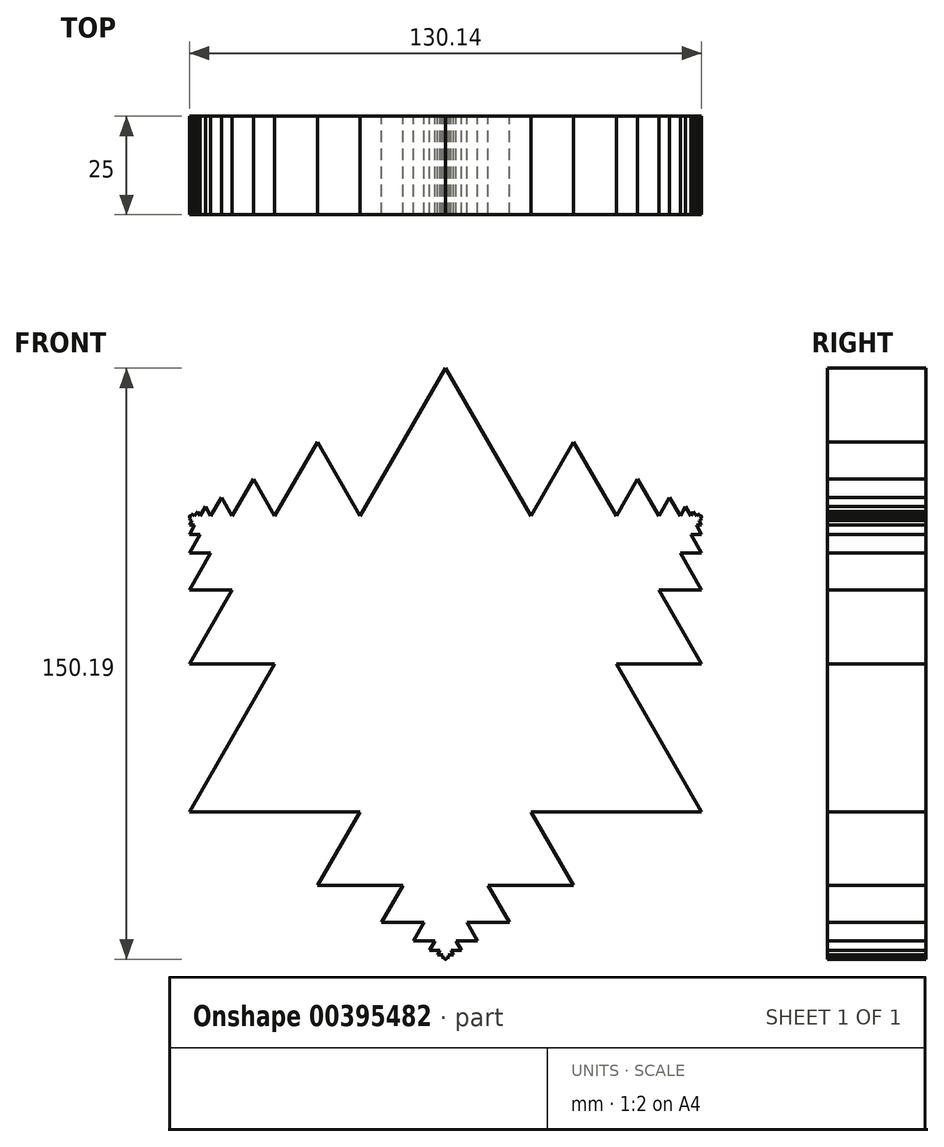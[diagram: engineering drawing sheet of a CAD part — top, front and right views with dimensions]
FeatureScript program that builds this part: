
annotation { "Feature Type Name" : "Feature", "Feature Type Description" : "" }
export const myFeature = defineFeature(function(context is Context, id is Id, definition is map)
    precondition{}
    {
        {
            var Q0;
            Q0=qCreatedBy(makeId("Front.planeOp"),FACE);
            var sketch = newSketch(context, id + "F0", { "sketchPlane" : qUnion([Q0])});
            skLineSegment(sketch, "E0.0", {"start": v(0, 75.13) * mm, "end": v(65.07, -37.57) * mm});
            skLineSegment(sketch, "E0.1", {"start": v(65.07, -37.57) * mm, "end": v(-65.07, -37.57) * mm});
            skLineSegment(sketch, "E0.2", {"start": v(-65.07, -37.57) * mm, "end": v(0, 75.13) * mm});
            skLineSegment(sketch, "E1.0", {"start": v(0, 0) * mm, "end": v(-65.07, 0) * mm});
            skLineSegment(sketch, "E1.1", {"start": v(-65.07, 0) * mm, "end": v(-32.53, 56.35) * mm});
            skLineSegment(sketch, "E1.2", {"start": v(-32.53, 56.35) * mm, "end": v(0, 0) * mm});
            skLineSegment(sketch, "E2.0", {"start": v(0, 0) * mm, "end": v(32.53, -56.35) * mm});
            skLineSegment(sketch, "E2.1", {"start": v(32.53, -56.35) * mm, "end": v(-32.53, -56.35) * mm});
            skLineSegment(sketch, "E2.2", {"start": v(-32.53, -56.35) * mm, "end": v(0, 0) * mm});
            skLineSegment(sketch, "E3.0", {"start": v(0, 0) * mm, "end": v(32.53, 56.35) * mm});
            skLineSegment(sketch, "E3.1", {"start": v(32.53, 56.35) * mm, "end": v(65.07, 0) * mm});
            skLineSegment(sketch, "E3.2", {"start": v(65.07, 0) * mm, "end": v(0, 0) * mm});
            skPoint(sketch, "E2.cCircle.center.orphan", {"position": v(0, -37.57) * mm});
            skPoint(sketch, "E3.cCircle.center.orphan", {"position": v(32.53, 18.78) * mm});
            skPoint(sketch, "E1.cCircle.center.orphan", {"position": v(-32.53, 18.78) * mm});
            skLineSegment(sketch, "E4.0", {"start": v(-32.53, 18.78) * mm, "end": v(-65.07, 18.78) * mm});
            skLineSegment(sketch, "E4.1", {"start": v(-65.07, 18.78) * mm, "end": v(-48.8, 46.96) * mm});
            skLineSegment(sketch, "E4.2", {"start": v(-48.8, 46.96) * mm, "end": v(-32.53, 18.78) * mm});
            skLineSegment(sketch, "E5.0", {"start": v(-32.53, 18.78) * mm, "end": v(-16.27, 46.96) * mm});
            skLineSegment(sketch, "E5.1", {"start": v(-16.27, 46.96) * mm, "end": v(0, 18.78) * mm});
            skLineSegment(sketch, "E5.2", {"start": v(0, 18.78) * mm, "end": v(-32.53, 18.78) * mm});
            skLineSegment(sketch, "E6.0", {"start": v(-32.53, 18.78) * mm, "end": v(-16.27, -9.4) * mm});
            skLineSegment(sketch, "E6.1", {"start": v(-16.27, -9.4) * mm, "end": v(-48.8, -9.4) * mm});
            skLineSegment(sketch, "E6.2", {"start": v(-48.8, -9.4) * mm, "end": v(-32.53, 18.78) * mm});
            skLineSegment(sketch, "E7.0", {"start": v(0, -37.57) * mm, "end": v(16.27, -65.74) * mm});
            skLineSegment(sketch, "E7.1", {"start": v(16.27, -65.74) * mm, "end": v(-16.27, -65.74) * mm});
            skLineSegment(sketch, "E7.2", {"start": v(-16.27, -65.74) * mm, "end": v(0, -37.57) * mm});
            skLineSegment(sketch, "E8.0", {"start": v(0, -37.57) * mm, "end": v(-32.53, -37.57) * mm});
            skLineSegment(sketch, "E8.1", {"start": v(-32.53, -37.57) * mm, "end": v(-16.27, -9.4) * mm});
            skLineSegment(sketch, "E8.2", {"start": v(-16.27, -9.4) * mm, "end": v(0, -37.57) * mm});
            skLineSegment(sketch, "E9.0", {"start": v(0, -37.57) * mm, "end": v(16.27, -9.4) * mm});
            skLineSegment(sketch, "E9.1", {"start": v(16.27, -9.4) * mm, "end": v(32.53, -37.57) * mm});
            skLineSegment(sketch, "E9.2", {"start": v(32.53, -37.57) * mm, "end": v(0, -37.57) * mm});
            skLineSegment(sketch, "E10.0", {"start": v(32.53, 18.78) * mm, "end": v(48.8, -9.4) * mm});
            skLineSegment(sketch, "E10.1", {"start": v(48.8, -9.4) * mm, "end": v(16.27, -9.4) * mm});
            skLineSegment(sketch, "E10.2", {"start": v(16.27, -9.4) * mm, "end": v(32.53, 18.78) * mm});
            skLineSegment(sketch, "E11.0", {"start": v(32.53, 18.78) * mm, "end": v(0, 18.78) * mm});
            skLineSegment(sketch, "E11.1", {"start": v(0, 18.78) * mm, "end": v(16.27, 46.96) * mm});
            skLineSegment(sketch, "E11.2", {"start": v(16.27, 46.96) * mm, "end": v(32.53, 18.78) * mm});
            skLineSegment(sketch, "E12.0", {"start": v(32.53, 18.78) * mm, "end": v(48.8, 46.96) * mm});
            skLineSegment(sketch, "E12.1", {"start": v(48.8, 46.96) * mm, "end": v(65.07, 18.78) * mm});
            skLineSegment(sketch, "E12.2", {"start": v(65.07, 18.78) * mm, "end": v(32.53, 18.78) * mm});
            skPoint(sketch, "E4.cCircle.center.orphan", {"position": v(-48.8, 28.18) * mm});
            skPoint(sketch, "E12.cCircle.center.orphan", {"position": v(48.8, 28.18) * mm});
            skPoint(sketch, "E11.cCircle.center.orphan", {"position": v(16.27, 28.18) * mm});
            skPoint(sketch, "E5.cCircle.center.orphan", {"position": v(-16.27, 28.18) * mm});
            skPoint(sketch, "E6.cCircle.center.orphan", {"position": v(-32.53, 0) * mm});
            skPoint(sketch, "E7.cCircle.center.orphan", {"position": v(0, -56.35) * mm});
            skPoint(sketch, "E10.cCircle.center.orphan", {"position": v(32.53, 0) * mm});
            skPoint(sketch, "E9.cCircle.center.orphan", {"position": v(16.27, -28.18) * mm});
            skPoint(sketch, "E8.cCircle.center.orphan", {"position": v(-16.27, -28.18) * mm});
            skCircle(sketch, "E13.cCircle", {"center": v(-56.93, 32.87) * mm, "radius": 9.4 * mm, "construction": true});
            skLineSegment(sketch, "E13.0", {"start": v(-48.8, 28.18) * mm, "end": v(-65.07, 28.18) * mm});
            skLineSegment(sketch, "E13.1", {"start": v(-65.07, 28.18) * mm, "end": v(-56.93, 42.26) * mm});
            skLineSegment(sketch, "E13.2", {"start": v(-56.93, 42.26) * mm, "end": v(-48.8, 28.18) * mm});
            skCircle(sketch, "E14.cCircle", {"center": v(0, -65.74) * mm, "radius": 9.4 * mm, "construction": true});
            skLineSegment(sketch, "E14.0", {"start": v(0, -56.35) * mm, "end": v(8.13, -70.44) * mm});
            skLineSegment(sketch, "E14.1", {"start": v(8.13, -70.44) * mm, "end": v(-8.13, -70.44) * mm});
            skLineSegment(sketch, "E14.2", {"start": v(-8.13, -70.44) * mm, "end": v(0, -56.35) * mm});
            skCircle(sketch, "E15.cCircle", {"center": v(56.93, 32.87) * mm, "radius": 9.4 * mm, "construction": true});
            skLineSegment(sketch, "E15.0", {"start": v(48.8, 28.18) * mm, "end": v(56.93, 42.26) * mm});
            skLineSegment(sketch, "E15.1", {"start": v(56.93, 42.26) * mm, "end": v(65.07, 28.18) * mm});
            skLineSegment(sketch, "E15.2", {"start": v(65.07, 28.18) * mm, "end": v(48.8, 28.18) * mm});
            skCircle(sketch, "E16.cCircle", {"center": v(-61, 35.22) * mm, "radius": 4.7 * mm, "construction": true});
            skLineSegment(sketch, "E16.0", {"start": v(-56.93, 32.87) * mm, "end": v(-65.07, 32.87) * mm});
            skLineSegment(sketch, "E16.1", {"start": v(-65.07, 32.87) * mm, "end": v(-61, 39.92) * mm});
            skLineSegment(sketch, "E16.2", {"start": v(-61, 39.92) * mm, "end": v(-56.93, 32.87) * mm});
            skCircle(sketch, "E17.cCircle", {"center": v(-63.04, 36.4) * mm, "radius": 2.35 * mm, "construction": true});
            skLineSegment(sketch, "E17.0", {"start": v(-61, 35.22) * mm, "end": v(-65.07, 35.22) * mm});
            skLineSegment(sketch, "E17.1", {"start": v(-65.07, 35.22) * mm, "end": v(-63.04, 38.74) * mm});
            skLineSegment(sketch, "E17.2", {"start": v(-63.04, 38.74) * mm, "end": v(-61, 35.22) * mm});
            skCircle(sketch, "E18.cCircle", {"center": v(-64.05, 36.98) * mm, "radius": 1.17 * mm, "construction": true});
            skLineSegment(sketch, "E18.0", {"start": v(-63.04, 36.4) * mm, "end": v(-65.07, 36.4) * mm});
            skLineSegment(sketch, "E18.1", {"start": v(-65.07, 36.4) * mm, "end": v(-64.05, 38.15) * mm});
            skLineSegment(sketch, "E18.2", {"start": v(-64.05, 38.15) * mm, "end": v(-63.04, 36.4) * mm});
            skCircle(sketch, "E19.cCircle", {"center": v(-64.56, 37.27) * mm, "radius": 0.59 * mm, "construction": true});
            skLineSegment(sketch, "E19.0", {"start": v(-64.05, 36.98) * mm, "end": v(-65.07, 36.98) * mm});
            skLineSegment(sketch, "E19.1", {"start": v(-65.07, 36.98) * mm, "end": v(-64.56, 37.86) * mm});
            skLineSegment(sketch, "E19.2", {"start": v(-64.56, 37.86) * mm, "end": v(-64.05, 36.98) * mm});
            skCircle(sketch, "E20.cCircle", {"center": v(-64.81, 37.42) * mm, "radius": 0.3 * mm, "construction": true});
            skLineSegment(sketch, "E20.0", {"start": v(-64.56, 37.27) * mm, "end": v(-65.07, 37.27) * mm});
            skLineSegment(sketch, "E20.1", {"start": v(-65.07, 37.27) * mm, "end": v(-64.81, 37.71) * mm});
            skLineSegment(sketch, "E20.2", {"start": v(-64.81, 37.71) * mm, "end": v(-64.56, 37.27) * mm});
            skCircle(sketch, "E21.cCircle", {"center": v(-64.94, 37.5) * mm, "radius": 0.15 * mm, "construction": true});
            skLineSegment(sketch, "E21.0", {"start": v(-64.81, 37.42) * mm, "end": v(-65.07, 37.42) * mm});
            skLineSegment(sketch, "E21.1", {"start": v(-65.07, 37.42) * mm, "end": v(-64.94, 37.64) * mm});
            skLineSegment(sketch, "E21.2", {"start": v(-64.94, 37.64) * mm, "end": v(-64.81, 37.42) * mm});
            skCircle(sketch, "E22.cCircle", {"center": v(0, -70.44) * mm, "radius": 4.7 * mm, "construction": true});
            skLineSegment(sketch, "E22.0", {"start": v(0, -65.74) * mm, "end": v(4.07, -72.79) * mm});
            skLineSegment(sketch, "E22.1", {"start": v(4.07, -72.79) * mm, "end": v(-4.07, -72.79) * mm});
            skLineSegment(sketch, "E22.2", {"start": v(-4.07, -72.79) * mm, "end": v(0, -65.74) * mm});
            skCircle(sketch, "E23.cCircle", {"center": v(0, -72.79) * mm, "radius": 2.35 * mm, "construction": true});
            skLineSegment(sketch, "E23.0", {"start": v(0, -70.44) * mm, "end": v(2.03, -73.96) * mm});
            skLineSegment(sketch, "E23.1", {"start": v(2.03, -73.96) * mm, "end": v(-2.03, -73.96) * mm});
            skLineSegment(sketch, "E23.2", {"start": v(-2.03, -73.96) * mm, "end": v(0, -70.44) * mm});
            skCircle(sketch, "E24.cCircle", {"center": v(0, -73.96) * mm, "radius": 1.17 * mm, "construction": true});
            skLineSegment(sketch, "E24.0", {"start": v(0, -72.79) * mm, "end": v(1.02, -74.55) * mm});
            skLineSegment(sketch, "E24.1", {"start": v(1.02, -74.55) * mm, "end": v(-1.02, -74.55) * mm});
            skLineSegment(sketch, "E24.2", {"start": v(-1.02, -74.55) * mm, "end": v(0, -72.79) * mm});
            skCircle(sketch, "E25.cCircle", {"center": v(0, -74.55) * mm, "radius": 0.59 * mm, "construction": true});
            skLineSegment(sketch, "E25.0", {"start": v(0, -73.96) * mm, "end": v(0.5, -74.84) * mm});
            skLineSegment(sketch, "E25.1", {"start": v(0.5, -74.84) * mm, "end": v(-0.5, -74.84) * mm});
            skLineSegment(sketch, "E25.2", {"start": v(-0.5, -74.84) * mm, "end": v(0, -73.96) * mm});
            skCircle(sketch, "E26.cCircle", {"center": v(0, -74.84) * mm, "radius": 0.3 * mm, "construction": true});
            skLineSegment(sketch, "E26.0", {"start": v(0, -74.55) * mm, "end": v(0.25, -74.99) * mm});
            skLineSegment(sketch, "E26.1", {"start": v(0.25, -74.99) * mm, "end": v(-0.25, -74.99) * mm});
            skLineSegment(sketch, "E26.2", {"start": v(-0.25, -74.99) * mm, "end": v(0, -74.55) * mm});
            skCircle(sketch, "E27.cCircle", {"center": v(0, -74.99) * mm, "radius": 0.15 * mm, "construction": true});
            skLineSegment(sketch, "E27.0", {"start": v(0, -74.84) * mm, "end": v(0.13, -75.06) * mm});
            skLineSegment(sketch, "E27.1", {"start": v(0.13, -75.06) * mm, "end": v(-0.13, -75.06) * mm});
            skLineSegment(sketch, "E27.2", {"start": v(-0.13, -75.06) * mm, "end": v(0, -74.84) * mm});
            skCircle(sketch, "E28.cCircle", {"center": v(61, 35.22) * mm, "radius": 4.7 * mm, "construction": true});
            skLineSegment(sketch, "E28.0", {"start": v(56.93, 32.87) * mm, "end": v(61, 39.92) * mm});
            skLineSegment(sketch, "E28.1", {"start": v(61, 39.92) * mm, "end": v(65.07, 32.87) * mm});
            skLineSegment(sketch, "E28.2", {"start": v(65.07, 32.87) * mm, "end": v(56.93, 32.87) * mm});
            skCircle(sketch, "E29.cCircle", {"center": v(63.04, 36.4) * mm, "radius": 2.35 * mm, "construction": true});
            skLineSegment(sketch, "E29.0", {"start": v(61, 35.22) * mm, "end": v(63.04, 38.74) * mm});
            skLineSegment(sketch, "E29.1", {"start": v(63.04, 38.74) * mm, "end": v(65.07, 35.22) * mm});
            skLineSegment(sketch, "E29.2", {"start": v(65.07, 35.22) * mm, "end": v(61, 35.22) * mm});
            skCircle(sketch, "E30.cCircle", {"center": v(64.05, 36.98) * mm, "radius": 1.17 * mm, "construction": true});
            skLineSegment(sketch, "E30.0", {"start": v(63.04, 36.4) * mm, "end": v(64.05, 38.15) * mm});
            skLineSegment(sketch, "E30.1", {"start": v(64.05, 38.15) * mm, "end": v(65.07, 36.4) * mm});
            skLineSegment(sketch, "E30.2", {"start": v(65.07, 36.4) * mm, "end": v(63.04, 36.4) * mm});
            skCircle(sketch, "E31.cCircle", {"center": v(64.56, 37.27) * mm, "radius": 0.59 * mm, "construction": true});
            skLineSegment(sketch, "E31.0", {"start": v(64.05, 36.98) * mm, "end": v(64.56, 37.86) * mm});
            skLineSegment(sketch, "E31.1", {"start": v(64.56, 37.86) * mm, "end": v(65.07, 36.98) * mm});
            skLineSegment(sketch, "E31.2", {"start": v(65.07, 36.98) * mm, "end": v(64.05, 36.98) * mm});
            skCircle(sketch, "E32.cCircle", {"center": v(64.81, 37.42) * mm, "radius": 0.3 * mm, "construction": true});
            skLineSegment(sketch, "E32.0", {"start": v(64.56, 37.27) * mm, "end": v(64.81, 37.71) * mm});
            skLineSegment(sketch, "E32.1", {"start": v(64.81, 37.71) * mm, "end": v(65.07, 37.27) * mm});
            skLineSegment(sketch, "E32.2", {"start": v(65.07, 37.27) * mm, "end": v(64.56, 37.27) * mm});
            skCircle(sketch, "E33.cCircle", {"center": v(64.94, 37.5) * mm, "radius": 0.15 * mm, "construction": true});
            skLineSegment(sketch, "E33.0", {"start": v(64.81, 37.42) * mm, "end": v(64.94, 37.64) * mm});
            skLineSegment(sketch, "E33.1", {"start": v(64.94, 37.64) * mm, "end": v(65.07, 37.42) * mm});
            skLineSegment(sketch, "E33.2", {"start": v(65.07, 37.42) * mm, "end": v(64.81, 37.42) * mm});
            skSolve(sketch);
        }
        {
            var Q0;
            {var subQ0=sQuery(id+"F0.wireOp",EDGE,"E12.1");var subQ2=sQuery(id+"F0.wireOp",EDGE,"E15.0");var subQ3=makeQuery(id+"F0.imprint","INTERSECT",VERTEX,{"derivedFrom":[subQ0,subQ2]});Q0=makeQuery(id+"F0.imprint","IMPRINT",FACE,{"disambiguationData":[TD([[makeQuery(id+"F0.imprint","IMPRINT",EDGE,{"disambiguationData":[TD([[subQ3,-1.0]])],"derivedFrom":subQ0}),-1.0]])]});}
            var Q1;
            {var subQ0=sQuery(id+"F0.wireOp",EDGE,"E10.0");var subQ1=sQuery(id+"F0.wireOp",EDGE,"E3.2");var subQ2=makeQuery(id+"F0.imprint","INTERSECT",VERTEX,{"derivedFrom":[subQ1,subQ0]});Q1=makeQuery(id+"F0.imprint","IMPRINT",FACE,{"disambiguationData":[TD([[makeQuery(id+"F0.imprint","IMPRINT",EDGE,{"disambiguationData":[TD([[subQ2,-1.0]])],"derivedFrom":subQ1}),-1.0]])]});}
            var Q2;
            {var subQ1=sQuery(id+"F0.wireOp",EDGE,"E1.0");var subQ3=sQuery(id+"F0.wireOp",EDGE,"E6.0");var subQ4=makeQuery(id+"F0.imprint","INTERSECT",VERTEX,{"derivedFrom":[subQ1,subQ3]});Q2=makeQuery(id+"F0.imprint","IMPRINT",FACE,{"disambiguationData":[TD([[makeQuery(id+"F0.imprint","IMPRINT",EDGE,{"disambiguationData":[TD([[subQ4,1.0]])],"derivedFrom":subQ1}),-1.0]])]});}
            var Q3;
            {var subQ3=sQuery(id+"F0.wireOp",EDGE,"E15.2");var subQ5=sQuery(id+"F0.wireOp",EDGE,"E15.1");var subQ6=makeQuery(id+"F0.imprint","INTERSECT",VERTEX,{"derivedFrom":[subQ5,subQ3]});Q3=makeQuery(id+"F0.imprint","IMPRINT",FACE,{"disambiguationData":[TD([[makeQuery(id+"F0.imprint","IMPRINT",EDGE,{"disambiguationData":[TD([[subQ6,1.0]])],"derivedFrom":subQ5}),-1.0]])]});}
            var Q4;
            {var subQ1=sQuery(id+"F0.wireOp",EDGE,"E3.0");var subQ3=sQuery(id+"F0.wireOp",EDGE,"E11.0");var subQ4=makeQuery(id+"F0.imprint","INTERSECT",VERTEX,{"derivedFrom":[subQ1,subQ3]});Q4=makeQuery(id+"F0.imprint","IMPRINT",FACE,{"disambiguationData":[TD([[makeQuery(id+"F0.imprint","IMPRINT",EDGE,{"disambiguationData":[TD([[subQ4,1.0]])],"derivedFrom":subQ1}),-1.0]])]});}
            var Q5;
            {var subQ3=sQuery(id+"F0.wireOp",EDGE,"E12.2");var subQ5=sQuery(id+"F0.wireOp",EDGE,"E12.1");var subQ6=makeQuery(id+"F0.imprint","INTERSECT",VERTEX,{"derivedFrom":[subQ5,subQ3]});Q5=makeQuery(id+"F0.imprint","IMPRINT",FACE,{"disambiguationData":[TD([[makeQuery(id+"F0.imprint","IMPRINT",EDGE,{"disambiguationData":[TD([[subQ6,1.0]])],"derivedFrom":subQ5}),-1.0]])]});}
            var Q6;
            {var subQ5=sQuery(id+"F0.wireOp",EDGE,"E6.1");Q6=makeQuery(id+"F0.imprint","IMPRINT",FACE,{"disambiguationData":[TD([[makeQuery(id+"F0.imprint","IMPRINT",EDGE,{"derivedFrom":subQ5}),-1.0]])]});}
            var Q7;
            {var subQ0=sQuery(id+"F0.wireOp",EDGE,"E8.0");var subQ1=sQuery(id+"F0.wireOp",EDGE,"E2.2");var subQ2=makeQuery(id+"F0.imprint","INTERSECT",VERTEX,{"derivedFrom":[subQ1,subQ0]});Q7=makeQuery(id+"F0.imprint","IMPRINT",FACE,{"disambiguationData":[TD([[makeQuery(id+"F0.imprint","IMPRINT",EDGE,{"disambiguationData":[TD([[subQ2,-1.0]])],"derivedFrom":subQ1}),-1.0]])]});}
            var Q8;
            {var subQ0=sQuery(id+"F0.wireOp",EDGE,"E11.2");var subQ1=sQuery(id+"F0.wireOp",EDGE,"E3.0");var subQ2=makeQuery(id+"F0.imprint","INTERSECT",VERTEX,{"derivedFrom":[subQ1,subQ0]});Q8=makeQuery(id+"F0.imprint","IMPRINT",FACE,{"disambiguationData":[TD([[makeQuery(id+"F0.imprint","IMPRINT",EDGE,{"disambiguationData":[TD([[subQ2,1.0]])],"derivedFrom":subQ1}),-1.0]])]});}
            var Q9;
            {var subQ0=sQuery(id+"F0.wireOp",EDGE,"E4.1");var subQ2=sQuery(id+"F0.wireOp",EDGE,"E13.0");var subQ3=makeQuery(id+"F0.imprint","INTERSECT",VERTEX,{"derivedFrom":[subQ0,subQ2]});Q9=makeQuery(id+"F0.imprint","IMPRINT",FACE,{"disambiguationData":[TD([[makeQuery(id+"F0.imprint","IMPRINT",EDGE,{"disambiguationData":[TD([[subQ3,-1.0]])],"derivedFrom":subQ0}),-1.0]])]});}
            var Q10;
            {var subQ1=sQuery(id+"F0.wireOp",EDGE,"E1.0");var subQ3=sQuery(id+"F0.wireOp",EDGE,"E6.0");var subQ4=makeQuery(id+"F0.imprint","INTERSECT",VERTEX,{"derivedFrom":[subQ1,subQ3]});Q10=makeQuery(id+"F0.imprint","IMPRINT",FACE,{"disambiguationData":[TD([[makeQuery(id+"F0.imprint","IMPRINT",EDGE,{"disambiguationData":[TD([[subQ4,-1.0]])],"derivedFrom":subQ3}),1.0]])]});}
            var Q11;
            {var subQ0=sQuery(id+"F0.wireOp",EDGE,"E3.2");var subQ1=sQuery(id+"F0.wireOp",EDGE,"E3.1");var subQ2=makeQuery(id+"F0.imprint","INTERSECT",VERTEX,{"derivedFrom":[subQ1,subQ0]});Q11=makeQuery(id+"F0.imprint","IMPRINT",FACE,{"disambiguationData":[TD([[makeQuery(id+"F0.imprint","IMPRINT",EDGE,{"disambiguationData":[TD([[subQ2,1.0]])],"derivedFrom":subQ1}),-1.0]])]});}
            var Q12;
            {var subQ0=sQuery(id+"F0.wireOp",EDGE,"E6.2");var subQ1=sQuery(id+"F0.wireOp",EDGE,"E1.0");var subQ2=makeQuery(id+"F0.imprint","INTERSECT",VERTEX,{"derivedFrom":[subQ1,subQ0]});Q12=makeQuery(id+"F0.imprint","IMPRINT",FACE,{"disambiguationData":[TD([[makeQuery(id+"F0.imprint","IMPRINT",EDGE,{"disambiguationData":[TD([[subQ2,1.0]])],"derivedFrom":subQ1}),-1.0]])]});}
            var Q13;
            {var subQ5=sQuery(id+"F0.wireOp",EDGE,"E9.1");Q13=makeQuery(id+"F0.imprint","IMPRINT",FACE,{"disambiguationData":[TD([[makeQuery(id+"F0.imprint","IMPRINT",EDGE,{"derivedFrom":subQ5}),-1.0]])]});}
            var Q14;
            {var subQ0=sQuery(id+"F0.wireOp",EDGE,"E2.1");var subQ2=sQuery(id+"F0.wireOp",EDGE,"E7.0");var subQ3=makeQuery(id+"F0.imprint","INTERSECT",VERTEX,{"derivedFrom":[subQ0,subQ2]});Q14=makeQuery(id+"F0.imprint","IMPRINT",FACE,{"disambiguationData":[TD([[makeQuery(id+"F0.imprint","IMPRINT",EDGE,{"disambiguationData":[TD([[subQ3,-1.0]])],"derivedFrom":subQ0}),-1.0]])]});}
            var Q15;
            {var subQ5=sQuery(id+"F0.wireOp",EDGE,"E10.1");Q15=makeQuery(id+"F0.imprint","IMPRINT",FACE,{"disambiguationData":[TD([[makeQuery(id+"F0.imprint","IMPRINT",EDGE,{"derivedFrom":subQ5}),-1.0]])]});}
            var Q16;
            {var subQ3=sQuery(id+"F0.wireOp",EDGE,"E12.0");var subQ5=sQuery(id+"F0.wireOp",EDGE,"E12.1");var subQ6=makeQuery(id+"F0.imprint","INTERSECT",VERTEX,{"derivedFrom":[subQ3,subQ5]});Q16=makeQuery(id+"F0.imprint","IMPRINT",FACE,{"disambiguationData":[TD([[makeQuery(id+"F0.imprint","IMPRINT",EDGE,{"disambiguationData":[TD([[subQ6,1.0]])],"derivedFrom":subQ3}),-1.0]])]});}
            var Q17;
            {var subQ5=sQuery(id+"F0.wireOp",EDGE,"E8.1");Q17=makeQuery(id+"F0.imprint","IMPRINT",FACE,{"disambiguationData":[TD([[makeQuery(id+"F0.imprint","IMPRINT",EDGE,{"derivedFrom":subQ5}),-1.0]])]});}
            var Q18;
            {var subQ0=sQuery(id+"F0.wireOp",EDGE,"E3.1");var subQ2=sQuery(id+"F0.wireOp",EDGE,"E12.0");var subQ3=makeQuery(id+"F0.imprint","INTERSECT",VERTEX,{"derivedFrom":[subQ0,subQ2]});Q18=makeQuery(id+"F0.imprint","IMPRINT",FACE,{"disambiguationData":[TD([[makeQuery(id+"F0.imprint","IMPRINT",EDGE,{"disambiguationData":[TD([[subQ3,-1.0]])],"derivedFrom":subQ0}),-1.0]])]});}
            var Q19;
            {var subQ0=sQuery(id+"F0.wireOp",EDGE,"E2.2");var subQ1=sQuery(id+"F0.wireOp",EDGE,"E2.1");var subQ2=makeQuery(id+"F0.imprint","INTERSECT",VERTEX,{"derivedFrom":[subQ1,subQ0]});Q19=makeQuery(id+"F0.imprint","IMPRINT",FACE,{"disambiguationData":[TD([[makeQuery(id+"F0.imprint","IMPRINT",EDGE,{"disambiguationData":[TD([[subQ2,1.0]])],"derivedFrom":subQ1}),-1.0]])]});}
            var Q20;
            {var subQ0=sQuery(id+"F0.wireOp",EDGE,"E3.1");var subQ1=sQuery(id+"F0.wireOp",EDGE,"E3.0");var subQ2=makeQuery(id+"F0.imprint","INTERSECT",VERTEX,{"derivedFrom":[subQ1,subQ0]});Q20=makeQuery(id+"F0.imprint","IMPRINT",FACE,{"disambiguationData":[TD([[makeQuery(id+"F0.imprint","IMPRINT",EDGE,{"disambiguationData":[TD([[subQ2,1.0]])],"derivedFrom":subQ1}),-1.0]])]});}
            var Q21;
            {var subQ1=sQuery(id+"F0.wireOp",EDGE,"E2.0");var subQ3=sQuery(id+"F0.wireOp",EDGE,"E9.0");var subQ4=makeQuery(id+"F0.imprint","INTERSECT",VERTEX,{"derivedFrom":[subQ1,subQ3]});Q21=makeQuery(id+"F0.imprint","IMPRINT",FACE,{"disambiguationData":[TD([[makeQuery(id+"F0.imprint","IMPRINT",EDGE,{"disambiguationData":[TD([[subQ4,-1.0]])],"derivedFrom":subQ3}),1.0]])]});}
            var Q22;
            {var subQ0=sQuery(id+"F0.wireOp",EDGE,"E9.2");var subQ1=sQuery(id+"F0.wireOp",EDGE,"E2.0");var subQ2=makeQuery(id+"F0.imprint","INTERSECT",VERTEX,{"derivedFrom":[subQ1,subQ0]});Q22=makeQuery(id+"F0.imprint","IMPRINT",FACE,{"disambiguationData":[TD([[makeQuery(id+"F0.imprint","IMPRINT",EDGE,{"disambiguationData":[TD([[subQ2,1.0]])],"derivedFrom":subQ1}),-1.0]])]});}
            var Q23;
            {var subQ4=sQuery(id+"F0.wireOp",EDGE,"E5.1");Q23=makeQuery(id+"F0.imprint","IMPRINT",FACE,{"disambiguationData":[TD([[makeQuery(id+"F0.imprint","IMPRINT",EDGE,{"derivedFrom":subQ4}),1.0]])]});}
            var Q24;
            {var subQ4=sQuery(id+"F0.wireOp",EDGE,"E9.1");Q24=makeQuery(id+"F0.imprint","IMPRINT",FACE,{"disambiguationData":[TD([[makeQuery(id+"F0.imprint","IMPRINT",EDGE,{"derivedFrom":subQ4}),1.0]])]});}
            var Q25;
            {var subQ4=sQuery(id+"F0.wireOp",EDGE,"E6.1");Q25=makeQuery(id+"F0.imprint","IMPRINT",FACE,{"disambiguationData":[TD([[makeQuery(id+"F0.imprint","IMPRINT",EDGE,{"derivedFrom":subQ4}),1.0]])]});}
            var Q26;
            {var subQ0=sQuery(id+"F0.wireOp",EDGE,"E1.1");var subQ1=sQuery(id+"F0.wireOp",EDGE,"E1.0");var subQ2=makeQuery(id+"F0.imprint","INTERSECT",VERTEX,{"derivedFrom":[subQ1,subQ0]});Q26=makeQuery(id+"F0.imprint","IMPRINT",FACE,{"disambiguationData":[TD([[makeQuery(id+"F0.imprint","IMPRINT",EDGE,{"disambiguationData":[TD([[subQ2,1.0]])],"derivedFrom":subQ1}),-1.0]])]});}
            var Q27;
            {var subQ0=sQuery(id+"F0.wireOp",EDGE,"E5.0");var subQ1=sQuery(id+"F0.wireOp",EDGE,"E1.2");var subQ2=makeQuery(id+"F0.imprint","INTERSECT",VERTEX,{"derivedFrom":[subQ1,subQ0]});Q27=makeQuery(id+"F0.imprint","IMPRINT",FACE,{"disambiguationData":[TD([[makeQuery(id+"F0.imprint","IMPRINT",EDGE,{"disambiguationData":[TD([[subQ2,-1.0]])],"derivedFrom":subQ1}),-1.0]])]});}
            var Q28;
            {var subQ3=sQuery(id+"F0.wireOp",EDGE,"E4.0");var subQ5=sQuery(id+"F0.wireOp",EDGE,"E4.1");var subQ7=makeQuery(id+"F0.imprint","INTERSECT",VERTEX,{"derivedFrom":[subQ3,subQ5]});Q28=makeQuery(id+"F0.imprint","IMPRINT",FACE,{"disambiguationData":[TD([[makeQuery(id+"F0.imprint","IMPRINT",EDGE,{"disambiguationData":[TD([[subQ7,1.0]])],"derivedFrom":subQ3}),-1.0]])]});}
            var Q29;
            {var subQ3=sQuery(id+"F0.wireOp",EDGE,"E4.2");var subQ5=sQuery(id+"F0.wireOp",EDGE,"E4.1");var subQ6=makeQuery(id+"F0.imprint","INTERSECT",VERTEX,{"derivedFrom":[subQ5,subQ3]});Q29=makeQuery(id+"F0.imprint","IMPRINT",FACE,{"disambiguationData":[TD([[makeQuery(id+"F0.imprint","IMPRINT",EDGE,{"disambiguationData":[TD([[subQ6,1.0]])],"derivedFrom":subQ5}),-1.0]])]});}
            var Q30;
            {var subQ0=sQuery(id+"F0.wireOp",EDGE,"E1.2");var subQ1=sQuery(id+"F0.wireOp",EDGE,"E1.1");var subQ2=makeQuery(id+"F0.imprint","INTERSECT",VERTEX,{"derivedFrom":[subQ1,subQ0]});Q30=makeQuery(id+"F0.imprint","IMPRINT",FACE,{"disambiguationData":[TD([[makeQuery(id+"F0.imprint","IMPRINT",EDGE,{"disambiguationData":[TD([[subQ2,1.0]])],"derivedFrom":subQ1}),-1.0]])]});}
            var Q31;
            {var subQ0=sQuery(id+"F0.wireOp",EDGE,"E2.1");var subQ1=sQuery(id+"F0.wireOp",EDGE,"E2.0");var subQ2=makeQuery(id+"F0.imprint","INTERSECT",VERTEX,{"derivedFrom":[subQ1,subQ0]});Q31=makeQuery(id+"F0.imprint","IMPRINT",FACE,{"disambiguationData":[TD([[makeQuery(id+"F0.imprint","IMPRINT",EDGE,{"disambiguationData":[TD([[subQ2,1.0]])],"derivedFrom":subQ1}),-1.0]])]});}
            var Q32;
            {var subQ3=sQuery(id+"F0.wireOp",EDGE,"E7.0");var subQ5=sQuery(id+"F0.wireOp",EDGE,"E7.1");var subQ6=makeQuery(id+"F0.imprint","INTERSECT",VERTEX,{"derivedFrom":[subQ3,subQ5]});Q32=makeQuery(id+"F0.imprint","IMPRINT",FACE,{"disambiguationData":[TD([[makeQuery(id+"F0.imprint","IMPRINT",EDGE,{"disambiguationData":[TD([[subQ6,1.0]])],"derivedFrom":subQ3}),-1.0]])]});}
            var Q33;
            {var subQ3=sQuery(id+"F0.wireOp",EDGE,"E7.2");var subQ5=sQuery(id+"F0.wireOp",EDGE,"E7.1");var subQ6=makeQuery(id+"F0.imprint","INTERSECT",VERTEX,{"derivedFrom":[subQ5,subQ3]});Q33=makeQuery(id+"F0.imprint","IMPRINT",FACE,{"disambiguationData":[TD([[makeQuery(id+"F0.imprint","IMPRINT",EDGE,{"disambiguationData":[TD([[subQ6,1.0]])],"derivedFrom":subQ5}),-1.0]])]});}
            var Q34;
            {var subQ0=sQuery(id+"F0.wireOp",EDGE,"E1.1");var subQ2=sQuery(id+"F0.wireOp",EDGE,"E4.0");var subQ3=makeQuery(id+"F0.imprint","INTERSECT",VERTEX,{"derivedFrom":[subQ0,subQ2]});Q34=makeQuery(id+"F0.imprint","IMPRINT",FACE,{"disambiguationData":[TD([[makeQuery(id+"F0.imprint","IMPRINT",EDGE,{"disambiguationData":[TD([[subQ3,-1.0]])],"derivedFrom":subQ0}),-1.0]])]});}
            var Q35;
            {var subQ5=sQuery(id+"F0.wireOp",EDGE,"E11.1");Q35=makeQuery(id+"F0.imprint","IMPRINT",FACE,{"disambiguationData":[TD([[makeQuery(id+"F0.imprint","IMPRINT",EDGE,{"derivedFrom":subQ5}),-1.0]])]});}
            var Q36;
            {var subQ1=sQuery(id+"F0.wireOp",EDGE,"E2.0");var subQ3=sQuery(id+"F0.wireOp",EDGE,"E9.0");var subQ4=makeQuery(id+"F0.imprint","INTERSECT",VERTEX,{"derivedFrom":[subQ1,subQ3]});Q36=makeQuery(id+"F0.imprint","IMPRINT",FACE,{"disambiguationData":[TD([[makeQuery(id+"F0.imprint","IMPRINT",EDGE,{"disambiguationData":[TD([[subQ4,1.0]])],"derivedFrom":subQ1}),-1.0]])]});}
            var Q37;
            {var subQ5=sQuery(id+"F0.wireOp",EDGE,"E5.1");Q37=makeQuery(id+"F0.imprint","IMPRINT",FACE,{"disambiguationData":[TD([[makeQuery(id+"F0.imprint","IMPRINT",EDGE,{"derivedFrom":subQ5}),-1.0]])]});}
            var Q38;
            {var subQ1=sQuery(id+"F0.wireOp",EDGE,"E1.2");var subQ3=sQuery(id+"F0.wireOp",EDGE,"E5.2");var subQ4=makeQuery(id+"F0.imprint","INTERSECT",VERTEX,{"derivedFrom":[subQ1,subQ3]});Q38=makeQuery(id+"F0.imprint","IMPRINT",FACE,{"disambiguationData":[TD([[makeQuery(id+"F0.imprint","IMPRINT",EDGE,{"disambiguationData":[TD([[subQ4,1.0]])],"derivedFrom":subQ3}),1.0]])]});}
            var Q39;
            {var subQ3=sQuery(id+"F0.wireOp",EDGE,"E13.2");var subQ5=sQuery(id+"F0.wireOp",EDGE,"E13.1");var subQ6=makeQuery(id+"F0.imprint","INTERSECT",VERTEX,{"derivedFrom":[subQ5,subQ3]});Q39=makeQuery(id+"F0.imprint","IMPRINT",FACE,{"disambiguationData":[TD([[makeQuery(id+"F0.imprint","IMPRINT",EDGE,{"disambiguationData":[TD([[subQ6,1.0]])],"derivedFrom":subQ5}),-1.0]])]});}
            var Q40;
            {var subQ3=sQuery(id+"F0.wireOp",EDGE,"E14.2");var subQ5=sQuery(id+"F0.wireOp",EDGE,"E14.1");var subQ6=makeQuery(id+"F0.imprint","INTERSECT",VERTEX,{"derivedFrom":[subQ5,subQ3]});Q40=makeQuery(id+"F0.imprint","IMPRINT",FACE,{"disambiguationData":[TD([[makeQuery(id+"F0.imprint","IMPRINT",EDGE,{"disambiguationData":[TD([[subQ6,1.0]])],"derivedFrom":subQ5}),-1.0]])]});}
            var Q41;
            {var subQ3=sQuery(id+"F0.wireOp",EDGE,"E14.0");var subQ5=sQuery(id+"F0.wireOp",EDGE,"E14.1");var subQ6=makeQuery(id+"F0.imprint","INTERSECT",VERTEX,{"derivedFrom":[subQ3,subQ5]});Q41=makeQuery(id+"F0.imprint","IMPRINT",FACE,{"disambiguationData":[TD([[makeQuery(id+"F0.imprint","IMPRINT",EDGE,{"disambiguationData":[TD([[subQ6,1.0]])],"derivedFrom":subQ3}),-1.0]])]});}
            var Q42;
            {var subQ3=sQuery(id+"F0.wireOp",EDGE,"E15.0");var subQ5=sQuery(id+"F0.wireOp",EDGE,"E15.1");var subQ6=makeQuery(id+"F0.imprint","INTERSECT",VERTEX,{"derivedFrom":[subQ3,subQ5]});Q42=makeQuery(id+"F0.imprint","IMPRINT",FACE,{"disambiguationData":[TD([[makeQuery(id+"F0.imprint","IMPRINT",EDGE,{"disambiguationData":[TD([[subQ6,1.0]])],"derivedFrom":subQ3}),-1.0]])]});}
            var Q43;
            {var subQ3=sQuery(id+"F0.wireOp",EDGE,"E13.0");var subQ5=sQuery(id+"F0.wireOp",EDGE,"E13.1");var subQ7=makeQuery(id+"F0.imprint","INTERSECT",VERTEX,{"derivedFrom":[subQ3,subQ5]});Q43=makeQuery(id+"F0.imprint","IMPRINT",FACE,{"disambiguationData":[TD([[makeQuery(id+"F0.imprint","IMPRINT",EDGE,{"disambiguationData":[TD([[subQ7,1.0]])],"derivedFrom":subQ3}),-1.0]])]});}
            var Q44;
            {var subQ0=sQuery(id+"F0.wireOp",EDGE,"E7.1");var subQ2=sQuery(id+"F0.wireOp",EDGE,"E14.0");var subQ3=makeQuery(id+"F0.imprint","INTERSECT",VERTEX,{"derivedFrom":[subQ0,subQ2]});Q44=makeQuery(id+"F0.imprint","IMPRINT",FACE,{"disambiguationData":[TD([[makeQuery(id+"F0.imprint","IMPRINT",EDGE,{"disambiguationData":[TD([[subQ3,-1.0]])],"derivedFrom":subQ0}),-1.0]])]});}
            var Q45;
            {var subQ0=sQuery(id+"F0.wireOp",EDGE,"E14.1");var subQ2=sQuery(id+"F0.wireOp",EDGE,"E22.0");var subQ3=makeQuery(id+"F0.imprint","INTERSECT",VERTEX,{"derivedFrom":[subQ0,subQ2]});Q45=makeQuery(id+"F0.imprint","IMPRINT",FACE,{"disambiguationData":[TD([[makeQuery(id+"F0.imprint","IMPRINT",EDGE,{"disambiguationData":[TD([[subQ3,-1.0]])],"derivedFrom":subQ0}),-1.0]])]});}
            var Q46;
            {var subQ0=sQuery(id+"F0.wireOp",EDGE,"E13.1");var subQ2=sQuery(id+"F0.wireOp",EDGE,"E16.0");var subQ3=makeQuery(id+"F0.imprint","INTERSECT",VERTEX,{"derivedFrom":[subQ0,subQ2]});Q46=makeQuery(id+"F0.imprint","IMPRINT",FACE,{"disambiguationData":[TD([[makeQuery(id+"F0.imprint","IMPRINT",EDGE,{"disambiguationData":[TD([[subQ3,-1.0]])],"derivedFrom":subQ0}),-1.0]])]});}
            var Q47;
            {var subQ0=sQuery(id+"F0.wireOp",EDGE,"E15.1");var subQ2=sQuery(id+"F0.wireOp",EDGE,"E28.0");var subQ3=makeQuery(id+"F0.imprint","INTERSECT",VERTEX,{"derivedFrom":[subQ0,subQ2]});Q47=makeQuery(id+"F0.imprint","IMPRINT",FACE,{"disambiguationData":[TD([[makeQuery(id+"F0.imprint","IMPRINT",EDGE,{"disambiguationData":[TD([[subQ3,-1.0]])],"derivedFrom":subQ0}),-1.0]])]});}
            var Q48;
            {var subQ3=sQuery(id+"F0.wireOp",EDGE,"E22.0");var subQ5=sQuery(id+"F0.wireOp",EDGE,"E22.1");var subQ7=makeQuery(id+"F0.imprint","INTERSECT",VERTEX,{"derivedFrom":[subQ3,subQ5]});Q48=makeQuery(id+"F0.imprint","IMPRINT",FACE,{"disambiguationData":[TD([[makeQuery(id+"F0.imprint","IMPRINT",EDGE,{"disambiguationData":[TD([[subQ7,1.0]])],"derivedFrom":subQ3}),-1.0]])]});}
            var Q49;
            {var subQ3=sQuery(id+"F0.wireOp",EDGE,"E16.2");var subQ5=sQuery(id+"F0.wireOp",EDGE,"E16.1");var subQ6=makeQuery(id+"F0.imprint","INTERSECT",VERTEX,{"derivedFrom":[subQ5,subQ3]});Q49=makeQuery(id+"F0.imprint","IMPRINT",FACE,{"disambiguationData":[TD([[makeQuery(id+"F0.imprint","IMPRINT",EDGE,{"disambiguationData":[TD([[subQ6,1.0]])],"derivedFrom":subQ5}),-1.0]])]});}
            var Q50;
            {var subQ3=sQuery(id+"F0.wireOp",EDGE,"E28.0");var subQ5=sQuery(id+"F0.wireOp",EDGE,"E28.1");var subQ6=makeQuery(id+"F0.imprint","INTERSECT",VERTEX,{"derivedFrom":[subQ3,subQ5]});Q50=makeQuery(id+"F0.imprint","IMPRINT",FACE,{"disambiguationData":[TD([[makeQuery(id+"F0.imprint","IMPRINT",EDGE,{"disambiguationData":[TD([[subQ6,1.0]])],"derivedFrom":subQ3}),-1.0]])]});}
            var Q51;
            {var subQ3=sQuery(id+"F0.wireOp",EDGE,"E22.2");var subQ5=sQuery(id+"F0.wireOp",EDGE,"E22.1");var subQ6=makeQuery(id+"F0.imprint","INTERSECT",VERTEX,{"derivedFrom":[subQ5,subQ3]});Q51=makeQuery(id+"F0.imprint","IMPRINT",FACE,{"disambiguationData":[TD([[makeQuery(id+"F0.imprint","IMPRINT",EDGE,{"disambiguationData":[TD([[subQ6,1.0]])],"derivedFrom":subQ5}),-1.0]])]});}
            var Q52;
            {var subQ3=sQuery(id+"F0.wireOp",EDGE,"E28.2");var subQ5=sQuery(id+"F0.wireOp",EDGE,"E28.1");var subQ6=makeQuery(id+"F0.imprint","INTERSECT",VERTEX,{"derivedFrom":[subQ5,subQ3]});Q52=makeQuery(id+"F0.imprint","IMPRINT",FACE,{"disambiguationData":[TD([[makeQuery(id+"F0.imprint","IMPRINT",EDGE,{"disambiguationData":[TD([[subQ6,1.0]])],"derivedFrom":subQ5}),-1.0]])]});}
            var Q53;
            {var subQ0=sQuery(id+"F0.wireOp",EDGE,"E28.1");var subQ2=sQuery(id+"F0.wireOp",EDGE,"E29.0");var subQ3=makeQuery(id+"F0.imprint","INTERSECT",VERTEX,{"derivedFrom":[subQ0,subQ2]});Q53=makeQuery(id+"F0.imprint","IMPRINT",FACE,{"disambiguationData":[TD([[makeQuery(id+"F0.imprint","IMPRINT",EDGE,{"disambiguationData":[TD([[subQ3,-1.0]])],"derivedFrom":subQ0}),-1.0]])]});}
            var Q54;
            {var subQ3=sQuery(id+"F0.wireOp",EDGE,"E16.0");var subQ5=sQuery(id+"F0.wireOp",EDGE,"E16.1");var subQ6=makeQuery(id+"F0.imprint","INTERSECT",VERTEX,{"derivedFrom":[subQ3,subQ5]});Q54=makeQuery(id+"F0.imprint","IMPRINT",FACE,{"disambiguationData":[TD([[makeQuery(id+"F0.imprint","IMPRINT",EDGE,{"disambiguationData":[TD([[subQ6,1.0]])],"derivedFrom":subQ3}),-1.0]])]});}
            var Q55;
            {var subQ0=sQuery(id+"F0.wireOp",EDGE,"E22.1");var subQ2=sQuery(id+"F0.wireOp",EDGE,"E23.0");var subQ3=makeQuery(id+"F0.imprint","INTERSECT",VERTEX,{"derivedFrom":[subQ0,subQ2]});Q55=makeQuery(id+"F0.imprint","IMPRINT",FACE,{"disambiguationData":[TD([[makeQuery(id+"F0.imprint","IMPRINT",EDGE,{"disambiguationData":[TD([[subQ3,-1.0]])],"derivedFrom":subQ0}),-1.0]])]});}
            var Q56;
            {var subQ3=sQuery(id+"F0.wireOp",EDGE,"E29.2");var subQ5=sQuery(id+"F0.wireOp",EDGE,"E29.1");var subQ6=makeQuery(id+"F0.imprint","INTERSECT",VERTEX,{"derivedFrom":[subQ5,subQ3]});Q56=makeQuery(id+"F0.imprint","IMPRINT",FACE,{"disambiguationData":[TD([[makeQuery(id+"F0.imprint","IMPRINT",EDGE,{"disambiguationData":[TD([[subQ6,1.0]])],"derivedFrom":subQ5}),-1.0]])]});}
            var Q57;
            {var subQ3=sQuery(id+"F0.wireOp",EDGE,"E29.0");var subQ5=sQuery(id+"F0.wireOp",EDGE,"E29.1");var subQ6=makeQuery(id+"F0.imprint","INTERSECT",VERTEX,{"derivedFrom":[subQ3,subQ5]});Q57=makeQuery(id+"F0.imprint","IMPRINT",FACE,{"disambiguationData":[TD([[makeQuery(id+"F0.imprint","IMPRINT",EDGE,{"disambiguationData":[TD([[subQ6,1.0]])],"derivedFrom":subQ3}),-1.0]])]});}
            var Q58;
            {var subQ0=sQuery(id+"F0.wireOp",EDGE,"E29.1");var subQ2=sQuery(id+"F0.wireOp",EDGE,"E30.0");var subQ3=makeQuery(id+"F0.imprint","INTERSECT",VERTEX,{"derivedFrom":[subQ0,subQ2]});Q58=makeQuery(id+"F0.imprint","IMPRINT",FACE,{"disambiguationData":[TD([[makeQuery(id+"F0.imprint","IMPRINT",EDGE,{"disambiguationData":[TD([[subQ3,-1.0]])],"derivedFrom":subQ0}),-1.0]])]});}
            var Q59;
            {var subQ3=sQuery(id+"F0.wireOp",EDGE,"E23.2");var subQ5=sQuery(id+"F0.wireOp",EDGE,"E23.1");var subQ6=makeQuery(id+"F0.imprint","INTERSECT",VERTEX,{"derivedFrom":[subQ5,subQ3]});Q59=makeQuery(id+"F0.imprint","IMPRINT",FACE,{"disambiguationData":[TD([[makeQuery(id+"F0.imprint","IMPRINT",EDGE,{"disambiguationData":[TD([[subQ6,1.0]])],"derivedFrom":subQ5}),-1.0]])]});}
            var Q60;
            {var subQ3=sQuery(id+"F0.wireOp",EDGE,"E23.0");var subQ5=sQuery(id+"F0.wireOp",EDGE,"E23.1");var subQ6=makeQuery(id+"F0.imprint","INTERSECT",VERTEX,{"derivedFrom":[subQ3,subQ5]});Q60=makeQuery(id+"F0.imprint","IMPRINT",FACE,{"disambiguationData":[TD([[makeQuery(id+"F0.imprint","IMPRINT",EDGE,{"disambiguationData":[TD([[subQ6,1.0]])],"derivedFrom":subQ3}),-1.0]])]});}
            var Q61;
            {var subQ3=sQuery(id+"F0.wireOp",EDGE,"E17.0");var subQ5=sQuery(id+"F0.wireOp",EDGE,"E17.1");var subQ6=makeQuery(id+"F0.imprint","INTERSECT",VERTEX,{"derivedFrom":[subQ3,subQ5]});Q61=makeQuery(id+"F0.imprint","IMPRINT",FACE,{"disambiguationData":[TD([[makeQuery(id+"F0.imprint","IMPRINT",EDGE,{"disambiguationData":[TD([[subQ6,1.0]])],"derivedFrom":subQ3}),-1.0]])]});}
            var Q62;
            {var subQ0=sQuery(id+"F0.wireOp",EDGE,"E16.1");var subQ2=sQuery(id+"F0.wireOp",EDGE,"E17.0");var subQ3=makeQuery(id+"F0.imprint","INTERSECT",VERTEX,{"derivedFrom":[subQ0,subQ2]});Q62=makeQuery(id+"F0.imprint","IMPRINT",FACE,{"disambiguationData":[TD([[makeQuery(id+"F0.imprint","IMPRINT",EDGE,{"disambiguationData":[TD([[subQ3,-1.0]])],"derivedFrom":subQ0}),-1.0]])]});}
            var Q63;
            {var subQ3=sQuery(id+"F0.wireOp",EDGE,"E25.0");var subQ5=sQuery(id+"F0.wireOp",EDGE,"E25.1");var subQ6=makeQuery(id+"F0.imprint","INTERSECT",VERTEX,{"derivedFrom":[subQ3,subQ5]});Q63=makeQuery(id+"F0.imprint","IMPRINT",FACE,{"disambiguationData":[TD([[makeQuery(id+"F0.imprint","IMPRINT",EDGE,{"disambiguationData":[TD([[subQ6,1.0]])],"derivedFrom":subQ3}),-1.0]])]});}
            var Q64;
            {var subQ0=sQuery(id+"F0.wireOp",EDGE,"E23.1");var subQ2=sQuery(id+"F0.wireOp",EDGE,"E24.0");var subQ3=makeQuery(id+"F0.imprint","INTERSECT",VERTEX,{"derivedFrom":[subQ0,subQ2]});Q64=makeQuery(id+"F0.imprint","IMPRINT",FACE,{"disambiguationData":[TD([[makeQuery(id+"F0.imprint","IMPRINT",EDGE,{"disambiguationData":[TD([[subQ3,-1.0]])],"derivedFrom":subQ0}),-1.0]])]});}
            var Q65;
            {var subQ3=sQuery(id+"F0.wireOp",EDGE,"E24.0");var subQ5=sQuery(id+"F0.wireOp",EDGE,"E24.1");var subQ6=makeQuery(id+"F0.imprint","INTERSECT",VERTEX,{"derivedFrom":[subQ3,subQ5]});Q65=makeQuery(id+"F0.imprint","IMPRINT",FACE,{"disambiguationData":[TD([[makeQuery(id+"F0.imprint","IMPRINT",EDGE,{"disambiguationData":[TD([[subQ6,1.0]])],"derivedFrom":subQ3}),-1.0]])]});}
            var Q66;
            {var subQ3=sQuery(id+"F0.wireOp",EDGE,"E17.2");var subQ5=sQuery(id+"F0.wireOp",EDGE,"E17.1");var subQ6=makeQuery(id+"F0.imprint","INTERSECT",VERTEX,{"derivedFrom":[subQ5,subQ3]});Q66=makeQuery(id+"F0.imprint","IMPRINT",FACE,{"disambiguationData":[TD([[makeQuery(id+"F0.imprint","IMPRINT",EDGE,{"disambiguationData":[TD([[subQ6,1.0]])],"derivedFrom":subQ5}),-1.0]])]});}
            var Q67;
            {var subQ0=sQuery(id+"F0.wireOp",EDGE,"E24.1");var subQ2=sQuery(id+"F0.wireOp",EDGE,"E25.0");var subQ3=makeQuery(id+"F0.imprint","INTERSECT",VERTEX,{"derivedFrom":[subQ0,subQ2]});Q67=makeQuery(id+"F0.imprint","IMPRINT",FACE,{"disambiguationData":[TD([[makeQuery(id+"F0.imprint","IMPRINT",EDGE,{"disambiguationData":[TD([[subQ3,-1.0]])],"derivedFrom":subQ0}),-1.0]])]});}
            var Q68;
            {var subQ3=sQuery(id+"F0.wireOp",EDGE,"E25.2");var subQ5=sQuery(id+"F0.wireOp",EDGE,"E25.1");var subQ6=makeQuery(id+"F0.imprint","INTERSECT",VERTEX,{"derivedFrom":[subQ5,subQ3]});Q68=makeQuery(id+"F0.imprint","IMPRINT",FACE,{"disambiguationData":[TD([[makeQuery(id+"F0.imprint","IMPRINT",EDGE,{"disambiguationData":[TD([[subQ6,1.0]])],"derivedFrom":subQ5}),-1.0]])]});}
            var Q69;
            {var subQ3=sQuery(id+"F0.wireOp",EDGE,"E26.2");var subQ5=sQuery(id+"F0.wireOp",EDGE,"E26.1");var subQ7=makeQuery(id+"F0.imprint","INTERSECT",VERTEX,{"derivedFrom":[subQ5,subQ3]});Q69=makeQuery(id+"F0.imprint","IMPRINT",FACE,{"disambiguationData":[TD([[makeQuery(id+"F0.imprint","IMPRINT",EDGE,{"disambiguationData":[TD([[subQ7,1.0]])],"derivedFrom":subQ5}),-1.0]])]});}
            var Q70;
            {var subQ0=sQuery(id+"F0.wireOp",EDGE,"E30.1");var subQ2=sQuery(id+"F0.wireOp",EDGE,"E31.0");var subQ3=makeQuery(id+"F0.imprint","INTERSECT",VERTEX,{"derivedFrom":[subQ0,subQ2]});Q70=makeQuery(id+"F0.imprint","IMPRINT",FACE,{"disambiguationData":[TD([[makeQuery(id+"F0.imprint","IMPRINT",EDGE,{"disambiguationData":[TD([[subQ3,-1.0]])],"derivedFrom":subQ0}),-1.0]])]});}
            var Q71;
            {var subQ3=sQuery(id+"F0.wireOp",EDGE,"E18.0");var subQ5=sQuery(id+"F0.wireOp",EDGE,"E18.1");var subQ6=makeQuery(id+"F0.imprint","INTERSECT",VERTEX,{"derivedFrom":[subQ3,subQ5]});Q71=makeQuery(id+"F0.imprint","IMPRINT",FACE,{"disambiguationData":[TD([[makeQuery(id+"F0.imprint","IMPRINT",EDGE,{"disambiguationData":[TD([[subQ6,1.0]])],"derivedFrom":subQ3}),-1.0]])]});}
            var Q72;
            {var subQ0=sQuery(id+"F0.wireOp",EDGE,"E25.1");var subQ2=sQuery(id+"F0.wireOp",EDGE,"E26.0");var subQ3=makeQuery(id+"F0.imprint","INTERSECT",VERTEX,{"derivedFrom":[subQ0,subQ2]});Q72=makeQuery(id+"F0.imprint","IMPRINT",FACE,{"disambiguationData":[TD([[makeQuery(id+"F0.imprint","IMPRINT",EDGE,{"disambiguationData":[TD([[subQ3,-1.0]])],"derivedFrom":subQ0}),-1.0]])]});}
            var Q73;
            {var subQ3=sQuery(id+"F0.wireOp",EDGE,"E18.2");var subQ5=sQuery(id+"F0.wireOp",EDGE,"E18.1");var subQ6=makeQuery(id+"F0.imprint","INTERSECT",VERTEX,{"derivedFrom":[subQ5,subQ3]});Q73=makeQuery(id+"F0.imprint","IMPRINT",FACE,{"disambiguationData":[TD([[makeQuery(id+"F0.imprint","IMPRINT",EDGE,{"disambiguationData":[TD([[subQ6,1.0]])],"derivedFrom":subQ5}),-1.0]])]});}
            var Q74;
            {var subQ3=sQuery(id+"F0.wireOp",EDGE,"E30.0");var subQ5=sQuery(id+"F0.wireOp",EDGE,"E30.1");var subQ6=makeQuery(id+"F0.imprint","INTERSECT",VERTEX,{"derivedFrom":[subQ3,subQ5]});Q74=makeQuery(id+"F0.imprint","IMPRINT",FACE,{"disambiguationData":[TD([[makeQuery(id+"F0.imprint","IMPRINT",EDGE,{"disambiguationData":[TD([[subQ6,1.0]])],"derivedFrom":subQ3}),-1.0]])]});}
            var Q75;
            {var subQ0=sQuery(id+"F0.wireOp",EDGE,"E17.1");var subQ2=sQuery(id+"F0.wireOp",EDGE,"E18.0");var subQ3=makeQuery(id+"F0.imprint","INTERSECT",VERTEX,{"derivedFrom":[subQ0,subQ2]});Q75=makeQuery(id+"F0.imprint","IMPRINT",FACE,{"disambiguationData":[TD([[makeQuery(id+"F0.imprint","IMPRINT",EDGE,{"disambiguationData":[TD([[subQ3,-1.0]])],"derivedFrom":subQ0}),-1.0]])]});}
            var Q76;
            {var subQ3=sQuery(id+"F0.wireOp",EDGE,"E19.2");var subQ5=sQuery(id+"F0.wireOp",EDGE,"E19.1");var subQ6=makeQuery(id+"F0.imprint","INTERSECT",VERTEX,{"derivedFrom":[subQ5,subQ3]});Q76=makeQuery(id+"F0.imprint","IMPRINT",FACE,{"disambiguationData":[TD([[makeQuery(id+"F0.imprint","IMPRINT",EDGE,{"disambiguationData":[TD([[subQ6,1.0]])],"derivedFrom":subQ5}),-1.0]])]});}
            var Q77;
            {var subQ3=sQuery(id+"F0.wireOp",EDGE,"E26.0");var subQ5=sQuery(id+"F0.wireOp",EDGE,"E26.1");var subQ6=makeQuery(id+"F0.imprint","INTERSECT",VERTEX,{"derivedFrom":[subQ3,subQ5]});Q77=makeQuery(id+"F0.imprint","IMPRINT",FACE,{"disambiguationData":[TD([[makeQuery(id+"F0.imprint","IMPRINT",EDGE,{"disambiguationData":[TD([[subQ6,1.0]])],"derivedFrom":subQ3}),-1.0]])]});}
            var Q78;
            {var subQ3=sQuery(id+"F0.wireOp",EDGE,"E24.2");var subQ5=sQuery(id+"F0.wireOp",EDGE,"E24.1");var subQ6=makeQuery(id+"F0.imprint","INTERSECT",VERTEX,{"derivedFrom":[subQ5,subQ3]});Q78=makeQuery(id+"F0.imprint","IMPRINT",FACE,{"disambiguationData":[TD([[makeQuery(id+"F0.imprint","IMPRINT",EDGE,{"disambiguationData":[TD([[subQ6,1.0]])],"derivedFrom":subQ5}),-1.0]])]});}
            var Q79;
            {var subQ3=sQuery(id+"F0.wireOp",EDGE,"E31.0");var subQ5=sQuery(id+"F0.wireOp",EDGE,"E31.1");var subQ6=makeQuery(id+"F0.imprint","INTERSECT",VERTEX,{"derivedFrom":[subQ3,subQ5]});Q79=makeQuery(id+"F0.imprint","IMPRINT",FACE,{"disambiguationData":[TD([[makeQuery(id+"F0.imprint","IMPRINT",EDGE,{"disambiguationData":[TD([[subQ6,1.0]])],"derivedFrom":subQ3}),-1.0]])]});}
            var Q80;
            {var subQ0=sQuery(id+"F0.wireOp",EDGE,"E27.0");var subQ1=sQuery(id+"F0.wireOp",EDGE,"E26.1");var subQ2=makeQuery(id+"F0.imprint","INTERSECT",VERTEX,{"derivedFrom":[subQ1,subQ0]});Q80=makeQuery(id+"F0.imprint","IMPRINT",FACE,{"disambiguationData":[TD([[makeQuery(id+"F0.imprint","IMPRINT",EDGE,{"disambiguationData":[TD([[subQ2,-1.0]])],"derivedFrom":subQ1}),-1.0]])]});}
            var Q81;
            {var subQ0=sQuery(id+"F0.wireOp",EDGE,"E18.1");var subQ2=sQuery(id+"F0.wireOp",EDGE,"E19.0");var subQ3=makeQuery(id+"F0.imprint","INTERSECT",VERTEX,{"derivedFrom":[subQ0,subQ2]});Q81=makeQuery(id+"F0.imprint","IMPRINT",FACE,{"disambiguationData":[TD([[makeQuery(id+"F0.imprint","IMPRINT",EDGE,{"disambiguationData":[TD([[subQ3,-1.0]])],"derivedFrom":subQ0}),-1.0]])]});}
            var Q82;
            {var subQ3=sQuery(id+"F0.wireOp",EDGE,"E30.2");var subQ5=sQuery(id+"F0.wireOp",EDGE,"E30.1");var subQ6=makeQuery(id+"F0.imprint","INTERSECT",VERTEX,{"derivedFrom":[subQ5,subQ3]});Q82=makeQuery(id+"F0.imprint","IMPRINT",FACE,{"disambiguationData":[TD([[makeQuery(id+"F0.imprint","IMPRINT",EDGE,{"disambiguationData":[TD([[subQ6,1.0]])],"derivedFrom":subQ5}),-1.0]])]});}
            var Q83;
            {var subQ0=sQuery(id+"F0.wireOp",EDGE,"E21.0");var subQ1=sQuery(id+"F0.wireOp",EDGE,"E20.1");var subQ2=makeQuery(id+"F0.imprint","INTERSECT",VERTEX,{"derivedFrom":[subQ1,subQ0]});Q83=makeQuery(id+"F0.imprint","IMPRINT",FACE,{"disambiguationData":[TD([[makeQuery(id+"F0.imprint","IMPRINT",EDGE,{"disambiguationData":[TD([[subQ2,-1.0]])],"derivedFrom":subQ1}),-1.0]])]});}
            var Q84;
            {var subQ3=sQuery(id+"F0.wireOp",EDGE,"E32.0");var subQ5=sQuery(id+"F0.wireOp",EDGE,"E32.1");var subQ6=makeQuery(id+"F0.imprint","INTERSECT",VERTEX,{"derivedFrom":[subQ3,subQ5]});Q84=makeQuery(id+"F0.imprint","IMPRINT",FACE,{"disambiguationData":[TD([[makeQuery(id+"F0.imprint","IMPRINT",EDGE,{"disambiguationData":[TD([[subQ6,1.0]])],"derivedFrom":subQ3}),-1.0]])]});}
            var Q85;
            {var subQ3=sQuery(id+"F0.wireOp",EDGE,"E19.0");var subQ5=sQuery(id+"F0.wireOp",EDGE,"E19.1");var subQ6=makeQuery(id+"F0.imprint","INTERSECT",VERTEX,{"derivedFrom":[subQ3,subQ5]});Q85=makeQuery(id+"F0.imprint","IMPRINT",FACE,{"disambiguationData":[TD([[makeQuery(id+"F0.imprint","IMPRINT",EDGE,{"disambiguationData":[TD([[subQ6,1.0]])],"derivedFrom":subQ3}),-1.0]])]});}
            var Q86;
            {var subQ3=sQuery(id+"F0.wireOp",EDGE,"E31.2");var subQ5=sQuery(id+"F0.wireOp",EDGE,"E31.1");var subQ6=makeQuery(id+"F0.imprint","INTERSECT",VERTEX,{"derivedFrom":[subQ5,subQ3]});Q86=makeQuery(id+"F0.imprint","IMPRINT",FACE,{"disambiguationData":[TD([[makeQuery(id+"F0.imprint","IMPRINT",EDGE,{"disambiguationData":[TD([[subQ6,1.0]])],"derivedFrom":subQ5}),-1.0]])]});}
            var Q87;
            {var subQ5=sQuery(id+"F0.wireOp",EDGE,"E27.1");Q87=makeQuery(id+"F0.imprint","IMPRINT",FACE,{"disambiguationData":[TD([[makeQuery(id+"F0.imprint","IMPRINT",EDGE,{"derivedFrom":subQ5}),-1.0]])]});}
            var Q88;
            {var subQ3=sQuery(id+"F0.wireOp",EDGE,"E32.2");var subQ5=sQuery(id+"F0.wireOp",EDGE,"E32.1");var subQ7=makeQuery(id+"F0.imprint","INTERSECT",VERTEX,{"derivedFrom":[subQ5,subQ3]});Q88=makeQuery(id+"F0.imprint","IMPRINT",FACE,{"disambiguationData":[TD([[makeQuery(id+"F0.imprint","IMPRINT",EDGE,{"disambiguationData":[TD([[subQ7,1.0]])],"derivedFrom":subQ5}),-1.0]])]});}
            var Q89;
            {var subQ3=sQuery(id+"F0.wireOp",EDGE,"E20.0");var subQ5=sQuery(id+"F0.wireOp",EDGE,"E20.1");var subQ6=makeQuery(id+"F0.imprint","INTERSECT",VERTEX,{"derivedFrom":[subQ3,subQ5]});Q89=makeQuery(id+"F0.imprint","IMPRINT",FACE,{"disambiguationData":[TD([[makeQuery(id+"F0.imprint","IMPRINT",EDGE,{"disambiguationData":[TD([[subQ6,1.0]])],"derivedFrom":subQ3}),-1.0]])]});}
            var Q90;
            {var subQ0=sQuery(id+"F0.wireOp",EDGE,"E33.0");var subQ1=sQuery(id+"F0.wireOp",EDGE,"E32.1");var subQ2=makeQuery(id+"F0.imprint","INTERSECT",VERTEX,{"derivedFrom":[subQ1,subQ0]});Q90=makeQuery(id+"F0.imprint","IMPRINT",FACE,{"disambiguationData":[TD([[makeQuery(id+"F0.imprint","IMPRINT",EDGE,{"disambiguationData":[TD([[subQ2,-1.0]])],"derivedFrom":subQ1}),-1.0]])]});}
            var Q91;
            {var subQ3=sQuery(id+"F0.wireOp",EDGE,"E20.2");var subQ5=sQuery(id+"F0.wireOp",EDGE,"E20.1");var subQ7=makeQuery(id+"F0.imprint","INTERSECT",VERTEX,{"derivedFrom":[subQ5,subQ3]});Q91=makeQuery(id+"F0.imprint","IMPRINT",FACE,{"disambiguationData":[TD([[makeQuery(id+"F0.imprint","IMPRINT",EDGE,{"disambiguationData":[TD([[subQ7,1.0]])],"derivedFrom":subQ5}),-1.0]])]});}
            var Q92;
            {var subQ0=sQuery(id+"F0.wireOp",EDGE,"E19.1");var subQ2=sQuery(id+"F0.wireOp",EDGE,"E20.0");var subQ3=makeQuery(id+"F0.imprint","INTERSECT",VERTEX,{"derivedFrom":[subQ0,subQ2]});Q92=makeQuery(id+"F0.imprint","IMPRINT",FACE,{"disambiguationData":[TD([[makeQuery(id+"F0.imprint","IMPRINT",EDGE,{"disambiguationData":[TD([[subQ3,-1.0]])],"derivedFrom":subQ0}),-1.0]])]});}
            var Q93;
            {var subQ5=sQuery(id+"F0.wireOp",EDGE,"E33.1");Q93=makeQuery(id+"F0.imprint","IMPRINT",FACE,{"disambiguationData":[TD([[makeQuery(id+"F0.imprint","IMPRINT",EDGE,{"derivedFrom":subQ5}),-1.0]])]});}
            var Q94;
            {var subQ0=sQuery(id+"F0.wireOp",EDGE,"E31.1");var subQ2=sQuery(id+"F0.wireOp",EDGE,"E32.0");var subQ3=makeQuery(id+"F0.imprint","INTERSECT",VERTEX,{"derivedFrom":[subQ0,subQ2]});Q94=makeQuery(id+"F0.imprint","IMPRINT",FACE,{"disambiguationData":[TD([[makeQuery(id+"F0.imprint","IMPRINT",EDGE,{"disambiguationData":[TD([[subQ3,-1.0]])],"derivedFrom":subQ0}),-1.0]])]});}
            var Q95;
            {var subQ5=sQuery(id+"F0.wireOp",EDGE,"E21.1");Q95=makeQuery(id+"F0.imprint","IMPRINT",FACE,{"disambiguationData":[TD([[makeQuery(id+"F0.imprint","IMPRINT",EDGE,{"derivedFrom":subQ5}),-1.0]])]});}
            extrude(context, id + "F1", {"entities" : qUnion([Q0, Q1, Q2, Q3, Q4, Q5, Q6, Q7, Q8, Q9, Q10, Q11, Q12, Q13, Q14, Q15, Q16, Q17, Q18, Q19, Q20, Q21, Q22, Q23, Q24, Q25, Q26, Q27, Q28, Q29, Q30, Q31, Q32, Q33, Q34, Q35, Q36, Q37, Q38, Q39, Q40, Q41, Q42, Q43, Q44, Q45, Q46, Q47, Q48, Q49, Q50, Q51, Q52, Q53, Q54, Q55, Q56, Q57, Q58, Q59, Q60, Q61, Q62, Q63, Q64, Q65, Q66, Q67, Q68, Q69, Q70, Q71, Q72, Q73, Q74, Q75, Q76, Q77, Q78, Q79, Q80, Q81, Q82, Q83, Q84, Q85, Q86, Q87, Q88, Q89, Q90, Q91, Q92, Q93, Q94, Q95]), "depth" : 25 * mm});
        }
    });
